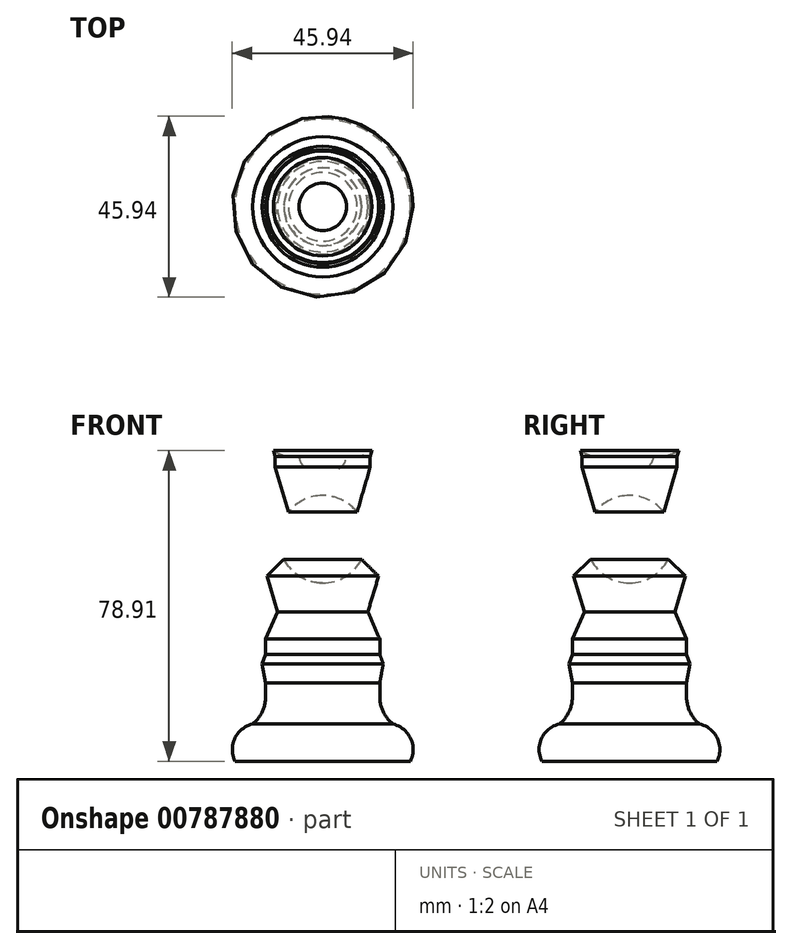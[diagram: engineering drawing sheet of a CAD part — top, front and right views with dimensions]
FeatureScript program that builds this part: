
annotation { "Feature Type Name" : "Feature", "Feature Type Description" : "" }
export const myFeature = defineFeature(function(context is Context, id is Id, definition is map)
    precondition{}
    {
        {
            var Q0;
            Q0=qCreatedBy(makeId("Front.planeOp"),FACE);
            var sketch = newSketch(context, id + "F0", { "sketchPlane" : qUnion([Q0])});
            skLineSegment(sketch, "E0", {"start": v(0, -19.86) * mm, "end": v(22.26, -19.86) * mm});
            skArc(sketch, "E1", {"start": v(22.26, -19.86) * mm, "mid": v(22.33, -14.06) * mm, "end": v(17.81, -10.41) * mm});
            skLineSegment(sketch, "E2", {"start": v(14.5, 11.19) * mm, "end": v(11.48, 18.12) * mm});
            skLineSegment(sketch, "E3", {"start": v(9.82, 31.33) * mm, "end": v(9.93, 31.34) * mm});
            skArc(sketch, "E4", {"start": v(0, 25.42) * mm, "mid": v(11.11, 36.53) * mm, "end": v(0, 47.64) * mm});
            skPoint(sketch, "E5.orphan", {"position": v(0, 31.05) * mm});
            skLineSegment(sketch, "E6", {"start": v(0, 47.64) * mm, "end": v(0, -19.86) * mm});
            skPoint(sketch, "E7.orphan", {"position": v(0, 61.42) * mm});
            skPoint(sketch, "E8.orphan", {"position": v(0, 54.8) * mm});
            skLineSegment(sketch, "E9", {"start": v(0, 54.8) * mm, "end": v(12.08, 54.86) * mm});
            skLineSegment(sketch, "E10", {"start": v(0, 54.8) * mm, "end": v(0, 36.53) * mm});
            skPoint(sketch, "E11.start.orphan", {"position": v(6.04, 54.83) * mm});
            skLineSegment(sketch, "E12", {"start": v(12.08, 54.86) * mm, "end": v(12.06, 57.53) * mm});
            skLineSegment(sketch, "E13", {"start": v(12.06, 57.53) * mm, "end": v(0, 57.47) * mm});
            skArc(sketch, "E14", {"start": v(6.03, 57.5) * mm, "mid": v(4.2, 61.29) * mm, "end": v(0, 61.42) * mm});
            skLineSegment(sketch, "E15", {"start": v(0, 61.42) * mm, "end": v(0, 47.64) * mm});
            skLineSegment(sketch, "E16", {"start": v(8.73, 43.4) * mm, "end": v(12.08, 54.86) * mm});
            skLineSegment(sketch, "E17", {"start": v(14.5, 11.19) * mm, "end": v(14.5, 7.23) * mm});
            skLineSegment(sketch, "E18", {"start": v(9.93, 31.34) * mm, "end": v(14.2, 27.15) * mm});
            skLineSegment(sketch, "E19", {"start": v(14.2, 27.15) * mm, "end": v(11.48, 18.12) * mm});
            skPoint(sketch, "E20.orphan", {"position": v(9.93, 21.69) * mm});
            skArc(sketch, "E21", {"start": v(14.5, -3.44) * mm, "mid": v(15.37, -7.3) * mm, "end": v(17.81, -10.41) * mm});
            skLineSegment(sketch, "E22.trimOffspring", {"start": v(14.5, 0) * mm, "end": v(14.5, -3.44) * mm});
            skLineSegment(sketch, "E23", {"start": v(14.5, 7.23) * mm, "end": v(15.39, 4.9) * mm});
            skLineSegment(sketch, "E24", {"start": v(15.39, 4.9) * mm, "end": v(14.5, 0) * mm});
            skLineSegment(sketch, "E25", {"start": v(12.06, 57.53) * mm, "end": v(12.51, 59.05) * mm});
            skArc(sketch, "E26", {"start": v(7.44, 57.5) * mm, "mid": v(10.1, 57.9) * mm, "end": v(12.51, 59.05) * mm});
            skSolve(sketch);
        }
        {
            var Q0;
            {var subQ3=sQuery(id+"F0.wireOp",EDGE,"E14");Q0=makeQuery(id+"F0.imprint","IMPRINT",FACE,{"disambiguationData":[TD([[makeQuery(id+"F0.imprint","IMPRINT",EDGE,{"derivedFrom":subQ3}),1.0]])]});}
            var Q1;
            {var subQ4=sQuery(id+"F0.wireOp",EDGE,"E9");Q1=makeQuery(id+"F0.imprint","IMPRINT",FACE,{"disambiguationData":[TD([[makeQuery(id+"F0.imprint","IMPRINT",EDGE,{"derivedFrom":subQ4}),-1.0]])]});}
            var Q2;
            {var subQ5=sQuery(id+"F0.wireOp",EDGE,"E9");Q2=makeQuery(id+"F0.imprint","IMPRINT",FACE,{"disambiguationData":[TD([[makeQuery(id+"F0.imprint","IMPRINT",EDGE,{"derivedFrom":subQ5}),1.0]])]});}
            var Q3;
            {var subQ0=sQuery(id+"F0.wireOp",EDGE,"E0");Q3=makeQuery(id+"F0.imprint","IMPRINT",FACE,{"disambiguationData":[TD([[makeQuery(id+"F0.imprint","IMPRINT",EDGE,{"derivedFrom":subQ0}),1.0]])]});}
            var Q4;
            {var subQ3=sQuery(id+"F0.wireOp",EDGE,"E10");Q4=makeQuery(id+"F0.imprint","IMPRINT",FACE,{"disambiguationData":[TD([[makeQuery(id+"F0.imprint","IMPRINT",EDGE,{"derivedFrom":subQ3}),1.0]])]});}
            var Q5;
            {var subQ0=sQuery(id+"F0.wireOp",EDGE,"lr2dX786-z29t-lWPI-k4dL-PSnEijAnIspZ");Q5=makeQuery(id+"F0.imprint","IMPRINT",FACE,{"disambiguationData":[TD([[makeQuery(id+"F0.imprint","IMPRINT",EDGE,{"derivedFrom":subQ0}),1.0]])]});}
            var Q6;
            {var subQ0=sQuery(id+"F0.wireOp",EDGE,"E25");Q6=makeQuery(id+"F0.imprint","IMPRINT",FACE,{"disambiguationData":[TD([[makeQuery(id+"F0.imprint","IMPRINT",EDGE,{"derivedFrom":subQ0}),1.0]])]});}
            var Q7;
            Q7=sQuery(id+"F0.wireOp",EDGE,"E6");
            revolve(context, id + "F1", {"surfaceOperationType" : NewSurfaceOperationType.NEW, "entities" : qUnion([Q0, Q1, Q2, Q3, Q4, Q5, Q6]), "axis" : qUnion([Q7]), "revolveType" : RevolveType.FULL});
        }
    });
